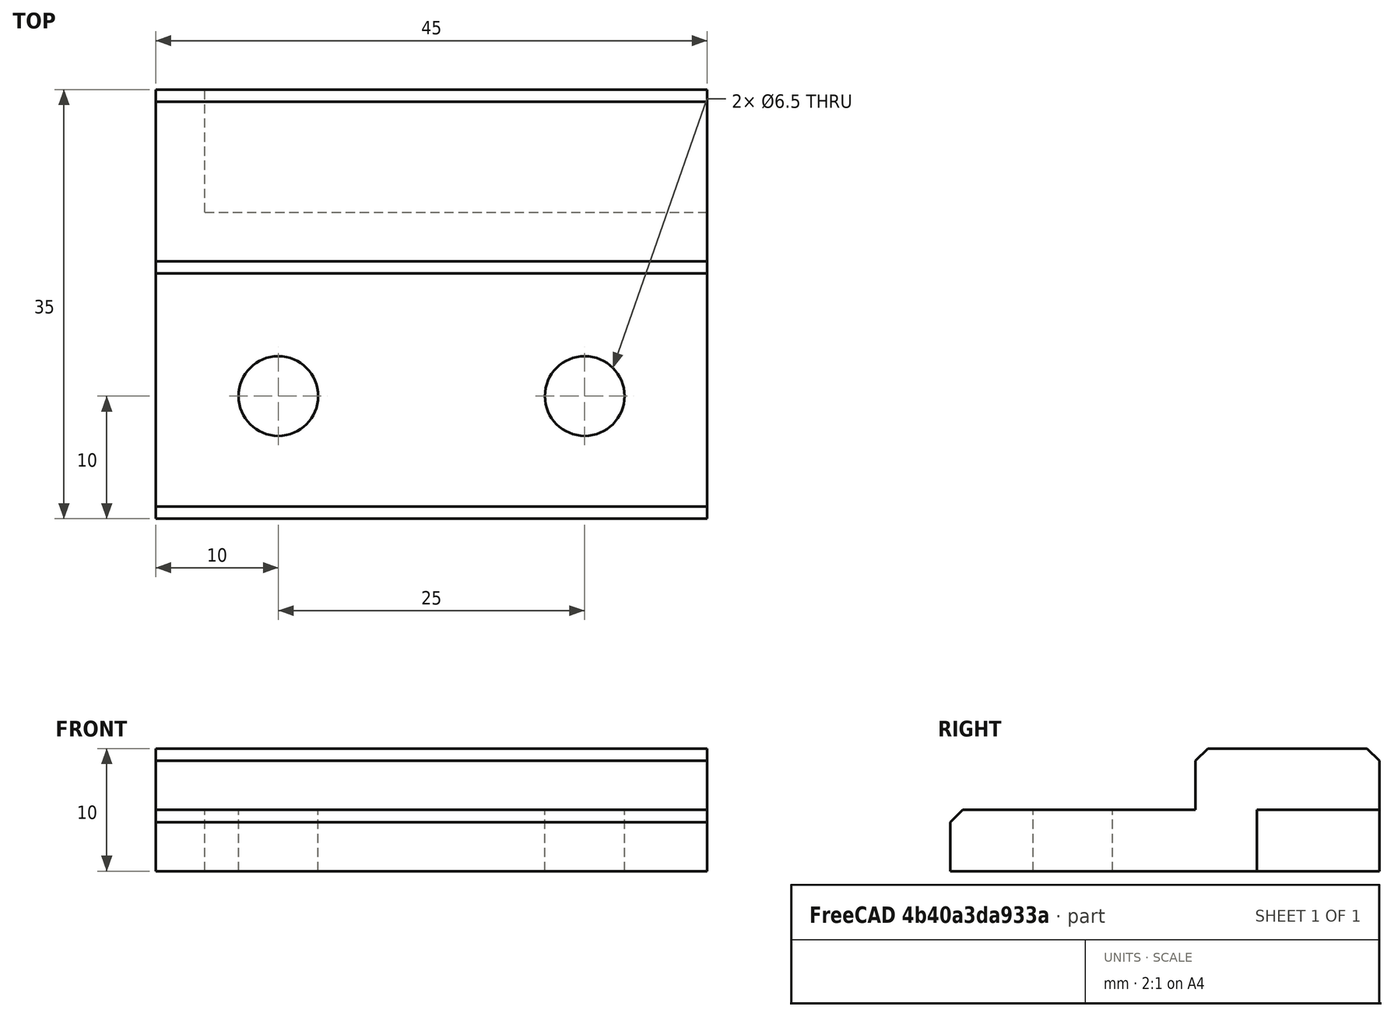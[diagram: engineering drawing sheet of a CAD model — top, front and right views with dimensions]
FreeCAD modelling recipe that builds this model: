
FCSTD DOCUMENT  (FreeCAD 0.14R3703 (Git))
Label: guia_cubeta_pos_izq
License: CC-BY 3.0
LicenseURL: http://creativecommons.org/licenses/by/3.0/
objects: Part::Chamfer×4, Part::Box×3, Part::Fuse×2, Part::Cylinder×2, Part::Cut×2, Part::Feature×1
note: 14 computed .brp shape members not serialized (recipe doc carries the construction recipe); baked Part::Feature solids carry a one-line shape summary decoded from their .brp

FEATURE [Part::Box] Box  label="Cubo"
  Height = 5
  Length = 45
  Width = 25
FEATURE [Part::Box] Box001  label="Cubo001"
  Height = 5
  Length = 45
  Placement = pos=(0,20,5) rot=(0,0,1;0rad)
  Width = 15
FEATURE [Part::Chamfer] Chamfer
  Base = -> Box
  Edges = 1 edges r=1: [Edge10]
FEATURE [Part::Chamfer] Chamfer001
  Base = -> Box001
  Edges = 1 edges r=1: [Edge10]
FEATURE [Part::Chamfer] Chamfer002
  Base = -> Chamfer001
  Edges = 1 edges r=1: [Edge13]
FEATURE [Part::Fuse] Fusion
  Base = -> Chamfer
  Tool = -> Chamfer002
FEATURE [Part::Cylinder] Cylinder  label="Cilindro"
  Angle = 360
  Height = 10
  Placement = pos=(10,10,0) rot=(0,0,1;0rad)
  Radius = 3.25
FEATURE [Part::Cut] Cut
  Base = -> Fusion
  Tool = -> Cylinder
FEATURE [Part::Cylinder] Cylinder001  label="Cilindro001"
  Angle = 360
  Height = 10
  Placement = pos=(35,10,0) rot=(0,0,1;0rad)
  Radius = 3.25
FEATURE [Part::Cut] Cut001
  Base = -> Cut
  Tool = -> Cylinder001
FEATURE [Part::Box] Box002  label="Cubo002"
  Height = 10
  Length = 4
  Placement = pos=(0,25,0) rot=(0,0,1;0rad)
  Width = 10
FEATURE [Part::Chamfer] Chamfer003
  Base = -> Box002
  Edges = 1 edges r=1: [Edge12]
FEATURE [Part::Fuse] Fusion001  label="guia_cubeta_pos_izq"
  Base = -> Cut001
  Tool = -> Chamfer003
FEATURE [Part::Feature] Fusion001001  label="guia_cubeta_pos_izq001"
  shape: bbox 45 x 35 x 10 mm, 16 faces (baked)
